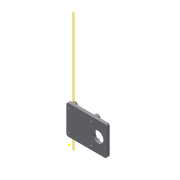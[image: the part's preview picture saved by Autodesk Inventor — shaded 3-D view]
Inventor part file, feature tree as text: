
AUTODESK INVENTOR PART (.ipt)
format: ipt  version: 2019.4 (Build 234330000, 330)  size: 196,096 bytes
history: native  units: mm
features: reference x10, other x6, extrude x3, sketch x2, plane x1, fillet x1, chamfer x1
ambient origin geometry x8: Origin, YZ Plane, XZ Plane, XY Plane, X Axis, Y Axis, Z Axis, Center Point
bodies: Solid1 (feature_tree)
feature tree (24):
  plane  "Work Plane1"
  extrude  "Extrusion1"  Depth=7.0mm
  extrude  "Extrusion2"  Depth=10.0mm
  sketch  "Sketch3"  dims[d2=70.0mm d3=4.9mm d4=4.9mm d5=4.9mm d6=4.9mm d7=10.0mm d8=10.0mm d9=10.0mm d10=10.0mm d15=7.0mm d16=0.0mm d17=25.0mm d18=5.0mm d19=0.0mm d20=0.0mm d23=5.0mm d42=3.0mm d43=3.0mm d45=3.0mm d46=10.0mm d47=0.0mm d48=0.0mm d49=4.0mm d50=2.0mm d51=45.0deg d52=6.75mm d54=6.75mm d55=12.0mm d56=2.9mm d57=2.9mm d58=2.9mm d59=2.9mm]
  fillet  "Fillet1"  Radius=4.9mm
  extrude  "Extrusion4"  Depth=10.0mm
  chamfer  "Chamfer1"  Distance=4.9mm
  sketch  "Sketch1"  dims[d0=50.0mm d1=7.0mm]
  reference  "Reference1"
  reference  "Reference2"
  reference  "Reference3"
  reference  "Reference4"
  reference  "Reference5"
  reference  "Reference6"
  reference  "Reference7"
  reference  "Reference8"
  reference  "Reference9"
  reference  "Reference10"
  other  "Assembly_neje_slide_y_wellplateholder_20mmrod.iam"
  other  "Neje_Base_Rod_double_20mm:1"
  other  "Assembly_neje_slide_plate:1"
  other  "Neje_Base_Rod_20mm:1"
  other  "Assembly_neje_slide_y_20mmrod.iam"
  other  "00_NEMA17:1"
